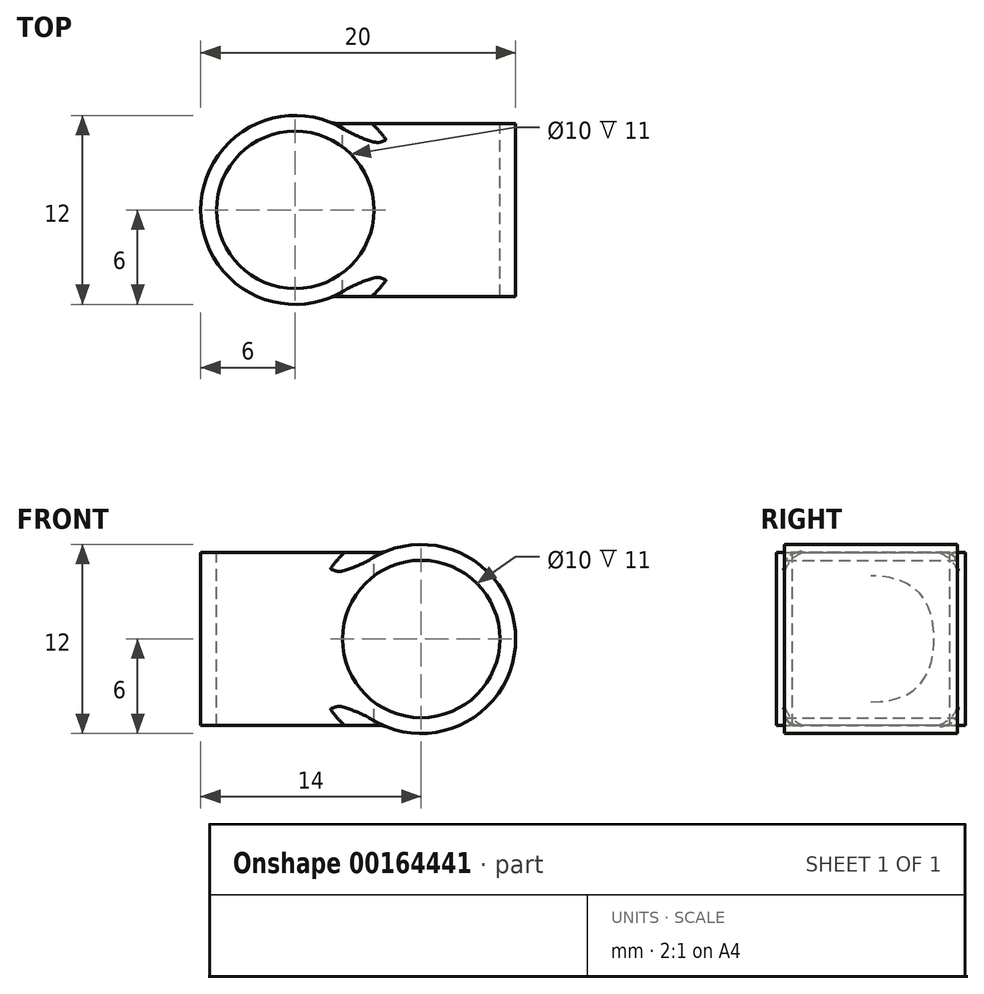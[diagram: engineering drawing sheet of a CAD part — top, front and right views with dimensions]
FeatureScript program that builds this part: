
annotation { "Feature Type Name" : "Feature", "Feature Type Description" : "" }
export const myFeature = defineFeature(function(context is Context, id is Id, definition is map)
    precondition{}
    {
        {
            assignVariable(context, id + "F0", {"name" : "diameter", "anyValue" : 10});
        }
        {
            var Q0;
            Q0=qCreatedBy(makeId("Front.planeOp"),FACE);
            var sketch = newSketch(context, id + "F1", { "sketchPlane" : qUnion([Q0])});
            skCircle(sketch, "E0", {"center": v(0, 0) * mm, "radius": 5 * mm});
            skCircle(sketch, "E1.0", {"center": v(0, 0) * mm, "radius": 6 * mm});
            skSolve(sketch);
        }
        {
            var Q0;
            Q0=qSketchRegion(id+"F1",true);
            var Q1;
            Q1=makeQuery(id+"F1.imprint","IMPRINT",FACE,{"disambiguationData":[TD([[makeQuery(id+"F1.imprint","IMPRINT",EDGE,{"derivedFrom":sQuery(id+"F1.wireOp",EDGE,"E0")}),1.0]])]});
            extrude(context, id + "F2", {"entities" : qUnion([Q0, Q1]), "endBound" : BoundingType.SYMMETRIC, "oppositeDirection" : true, "depth" : (getVariable(context, 'diameter') + 1) * mm});
        }
        {
            var Q0;
            Q0=qCreatedBy(makeId("Top.planeOp"),FACE);
            var sketch = newSketch(context, id + "F3", { "sketchPlane" : qUnion([Q0])});
            skCircle(sketch, "E2", {"center": v(-8, 0) * mm, "radius": 5 * mm});
            skCircle(sketch, "E3.0", {"center": v(-8, 0) * mm, "radius": 6 * mm});
            skSolve(sketch);
        }
        {
            var Q0;
            Q0 = qSketchRegion(id + "F3", true);
            var Q1;
            Q1=makeQuery(id+"F3.imprint","IMPRINT",FACE,{"disambiguationData":[TD([[makeQuery(id+"F3.imprint","IMPRINT",EDGE,{"derivedFrom":sQuery(id+"F3.wireOp",EDGE,"E2")}),1.0]])]});
            extrude(context, id + "F4", {"entities" : qUnion([Q0, Q1]), "endBound" : BoundingType.SYMMETRIC, "depth" : (getVariable(context, 'diameter') + 1) * mm});
        }
        {
            var Q0;
            Q0=makeQuery(id+"F2.opExtrude","SWEPT_BODY",BODY,{"disambiguationData":[OSD([sQuery(id+"F1.wireOp",EDGE,"E1.0")])]});
            var Q1;
            Q1=makeQuery(id+"F4.opExtrude","SWEPT_BODY",BODY,{"disambiguationData":[OSD([sQuery(id+"F3.wireOp",EDGE,"E3.0")])]});
            booleanBodies(context, id + "F5", {"operationType" : BooleanOperationType.UNION, "tools" : qUnion([Q0, Q1])});
        }
        {
            var Q0;
            Q0=makeQuery(id+"F1.imprint","IMPRINT",FACE,{"disambiguationData":[TD([[makeQuery(id+"F1.imprint","IMPRINT",EDGE,{"derivedFrom":sQuery(id+"F1.wireOp",EDGE,"E0")}),1.0]])]});
            extrude(context, id + "F6", {"entities" : qUnion([Q0]), "operationType" : NewBodyOperationType.REMOVE, "endBound" : BoundingType.THROUGH_ALL, "depth" : 50 * mm, "hasSecondDirection" : true, "secondDirectionOppositeDirection" : true, "secondDirectionDepth" : 32.5 * mm});
        }
        {
            var Q0;
            Q0=makeQuery(id+"F3.imprint","IMPRINT",FACE,{"disambiguationData":[TD([[makeQuery(id+"F3.imprint","IMPRINT",EDGE,{"derivedFrom":sQuery(id+"F3.wireOp",EDGE,"E2")}),1.0]])]});
            extrude(context, id + "F7", {"entities" : qUnion([Q0]), "operationType" : NewBodyOperationType.REMOVE, "endBound" : BoundingType.SYMMETRIC, "oppositeDirection" : true, "depth" : 50 * mm});
        }
        {
            var Q0;
            Q0=makeQuery(id+"F5.opBoolean","INTERSECT",EDGE,{"disambiguationData":[OD(2.0)],"derivedFrom":[makeQuery(id+"F2.opExtrude","SWEPT_FACE",FACE,{"disambiguationData":[OSD([sQuery(id+"F1.wireOp",EDGE,"E1.0")])]}),makeQuery(id+"F4.opExtrude","SWEPT_FACE",FACE,{"disambiguationData":[OSD([sQuery(id+"F3.wireOp",EDGE,"E3.0")])]})]});
            var Q1;
            Q1=makeQuery(id+"F5.opBoolean","INTERSECT",EDGE,{"disambiguationData":[OD(3.0)],"derivedFrom":[makeQuery(id+"F2.opExtrude","SWEPT_FACE",FACE,{"disambiguationData":[OSD([sQuery(id+"F1.wireOp",EDGE,"E1.0")])]}),makeQuery(id+"F4.opExtrude","SWEPT_FACE",FACE,{"disambiguationData":[OSD([sQuery(id+"F3.wireOp",EDGE,"E3.0")])]})]});
            var Q2;
            Q2=makeQuery(id+"F5.opBoolean","INTERSECT",EDGE,{"disambiguationData":[OD(1.0)],"derivedFrom":[makeQuery(id+"F2.opExtrude","SWEPT_FACE",FACE,{"disambiguationData":[OSD([sQuery(id+"F1.wireOp",EDGE,"E1.0")])]}),makeQuery(id+"F4.opExtrude","SWEPT_FACE",FACE,{"disambiguationData":[OSD([sQuery(id+"F3.wireOp",EDGE,"E3.0")])]})]});
            var Q3;
            Q3=makeQuery(id+"F5.opBoolean","INTERSECT",EDGE,{"derivedFrom":[makeQuery(id+"F2.opExtrude","SWEPT_FACE",FACE,{"disambiguationData":[OSD([sQuery(id+"F1.wireOp",EDGE,"E1.0")])]}),makeQuery(id+"F4.opExtrude","CAP_FACE",FACE,{"disambiguationData":[OSD([sQuery(id+"F3.wireOp",EDGE,"E3.0")])],"isStart":false})]});
            var Q4;
            Q4=makeQuery(id+"F5.opBoolean","INTERSECT",EDGE,{"derivedFrom":[makeQuery(id+"F2.opExtrude","CAP_FACE",FACE,{"disambiguationData":[OSD([sQuery(id+"F1.wireOp",EDGE,"E1.0")])],"isStart":true}),makeQuery(id+"F4.opExtrude","SWEPT_FACE",FACE,{"disambiguationData":[OSD([sQuery(id+"F3.wireOp",EDGE,"E3.0")])]})]});
            var Q5;
            Q5=makeQuery(id+"F5.opBoolean","INTERSECT",EDGE,{"disambiguationData":[OD(0.0)],"derivedFrom":[makeQuery(id+"F2.opExtrude","SWEPT_FACE",FACE,{"disambiguationData":[OSD([sQuery(id+"F1.wireOp",EDGE,"E1.0")])]}),makeQuery(id+"F4.opExtrude","SWEPT_FACE",FACE,{"disambiguationData":[OSD([sQuery(id+"F3.wireOp",EDGE,"E3.0")])]})]});
            var Q6;
            Q6=makeQuery(id+"F5.opBoolean","INTERSECT",EDGE,{"derivedFrom":[makeQuery(id+"F2.opExtrude","SWEPT_FACE",FACE,{"disambiguationData":[OSD([sQuery(id+"F1.wireOp",EDGE,"E1.0")])]}),makeQuery(id+"F4.opExtrude","CAP_FACE",FACE,{"disambiguationData":[OSD([sQuery(id+"F3.wireOp",EDGE,"E3.0")])],"isStart":true})]});
            var Q7;
            Q7=makeQuery(id+"F5.opBoolean","INTERSECT",EDGE,{"derivedFrom":[makeQuery(id+"F2.opExtrude","CAP_FACE",FACE,{"disambiguationData":[OSD([sQuery(id+"F1.wireOp",EDGE,"E1.0")])],"isStart":false}),makeQuery(id+"F4.opExtrude","SWEPT_FACE",FACE,{"disambiguationData":[OSD([sQuery(id+"F3.wireOp",EDGE,"E3.0")])]})]});
            fillet(context, id + "F8", {"entities" : qUnion([Q0, Q1, Q2, Q3, Q4, Q5, Q6, Q7]), "radius" : 1 * mm, "tangentPropagation" : true, "allowEdgeOverflow" : false});
        }
    });
